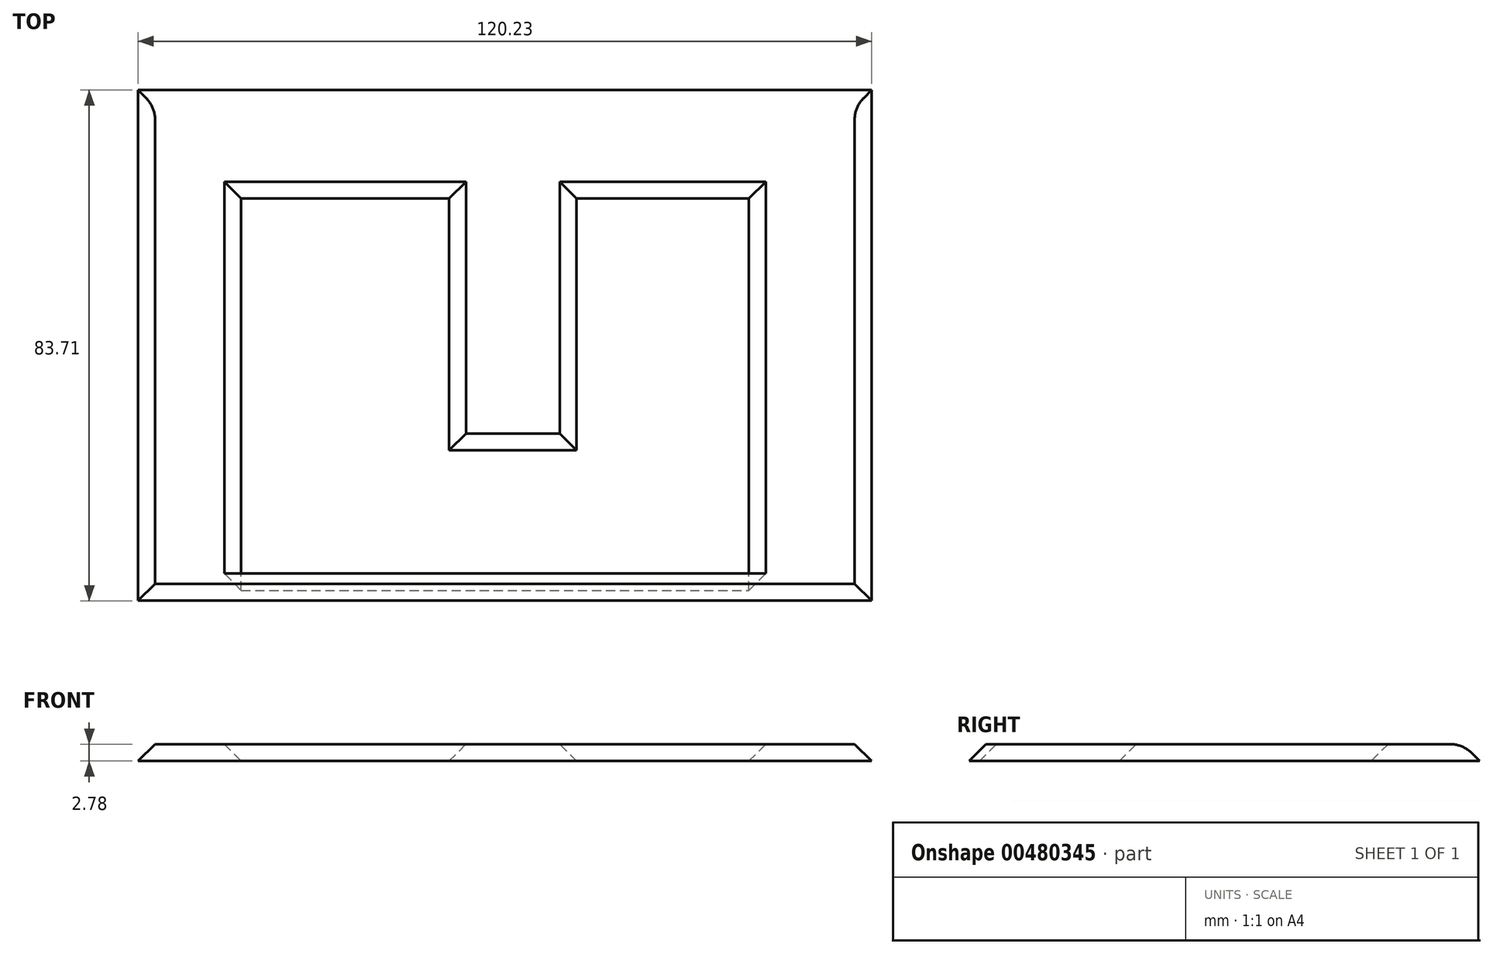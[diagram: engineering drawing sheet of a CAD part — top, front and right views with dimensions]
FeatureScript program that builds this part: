
annotation { "Feature Type Name" : "Feature", "Feature Type Description" : "" }
export const myFeature = defineFeature(function(context is Context, id is Id, definition is map)
    precondition{}
    {
        {
            var Q0;
            Q0=qCreatedBy(makeId("Top.planeOp"),FACE);
            var sketch = newSketch(context, id + "F0", { "sketchPlane" : qUnion([Q0])});
            skLineSegment(sketch, "E0.bottom", {"start": v(-59.68, 46.88) * mm, "end": v(65.17, 46.88) * mm});
            skLineSegment(sketch, "E0.top", {"start": v(-59.68, -41.44) * mm, "end": v(65.17, -41.44) * mm});
            skLineSegment(sketch, "E0.left", {"start": v(-59.68, 46.88) * mm, "end": v(-59.68, -41.44) * mm});
            skLineSegment(sketch, "E0.right", {"start": v(65.17, 46.88) * mm, "end": v(65.17, -41.44) * mm});
            skLineSegment(sketch, "E1.bottom", {"start": v(-38.17, 24.48) * mm, "end": v(-8.71, 24.48) * mm});
            skLineSegment(sketch, "E1.top", {"start": v(-38.17, -32.36) * mm, "end": v(40.45, -32.36) * mm});
            skLineSegment(sketch, "E1.left", {"start": v(-38.17, 24.48) * mm, "end": v(-38.17, -32.36) * mm});
            skLineSegment(sketch, "E1.right", {"start": v(40.45, 24.48) * mm, "end": v(40.45, -32.36) * mm});
            skLineSegment(sketch, "E2.top", {"start": v(-8.71, -16.8) * mm, "end": v(16.8, -16.8) * mm});
            skLineSegment(sketch, "E2.left", {"start": v(-8.71, 24.48) * mm, "end": v(-8.71, -16.8) * mm});
            skLineSegment(sketch, "E2.right", {"start": v(16.8, 24.48) * mm, "end": v(16.8, -16.8) * mm});
            skLineSegment(sketch, "E3.trimOffspring", {"start": v(16.8, 24.48) * mm, "end": v(40.45, 24.48) * mm});
            skSolve(sketch);
        }
        {
            var Q0;
            Q0=makeQuery(id+"F0.imprint","IMPRINT",FACE,{"disambiguationData":[TD([[makeQuery(id+"F0.imprint","IMPRINT",EDGE,{"derivedFrom":sQuery(id+"F0.wireOp",EDGE,"E0.bottom")}),-1.0]])]});
            extrude(context, id + "F1", {"entities" : qUnion([Q0]), "depth" : 2.78 * mm});
        }
        {
            var Q0;
            Q0=makeQuery(id+"F1.opExtrude","CAP_EDGE",EDGE,{"disambiguationData":[OSD([sQuery(id+"F0.wireOp",EDGE,"E0.right")])],"isStart":false});
            chamfer(context, id + "F2", {"entities" : qUnion([Q0]), "width" : 5.08 * mm, "tangentPropagation" : true});
        }
        {
            var Q0;
            Q0=makeQuery(id+"F1.opExtrude","CAP_EDGE",EDGE,{"disambiguationData":[OSD([sQuery(id+"F0.wireOp",EDGE,"E0.bottom")])],"isStart":false});
            chamfer(context, id + "F3", {"entities" : qUnion([Q0]), "width" : 5.08 * mm, "tangentPropagation" : true});
        }
        {
            var Q0;
            Q0=makeQuery(id+"F1.opExtrude","CAP_EDGE",EDGE,{"disambiguationData":[OSD([sQuery(id+"F0.wireOp",EDGE,"E0.left")])],"isStart":false});
            chamfer(context, id + "F4", {"entities" : qUnion([Q0]), "width" : 5.08 * mm, "tangentPropagation" : true});
        }
        {
            var Q0;
            Q0=makeQuery(id+"F1.opExtrude","CAP_EDGE",EDGE,{"disambiguationData":[OSD([sQuery(id+"F0.wireOp",EDGE,"E0.top")])],"isStart":false});
            chamfer(context, id + "F5", {"entities" : qUnion([Q0]), "width" : 5.08 * mm, "tangentPropagation" : true});
        }
        {
            var Q0;
            {var subQ0=sQuery(id+"F0.wireOp",EDGE,"E0.bottom");Q0=makeQuery(id+"F3.opChamfer","BLEND_EDGE",EDGE,{"blendedFrom":[makeQuery(id+"F1.opExtrude","CAP_EDGE",EDGE,{"disambiguationData":[OSD([subQ0])],"isStart":false}),makeQuery(id+"F1.opExtrude","CAP_FACE",FACE,{"disambiguationData":[OSD([subQ0,sQuery(id+"F0.wireOp",EDGE,"E0.top"),sQuery(id+"F0.wireOp",EDGE,"E0.left"),sQuery(id+"F0.wireOp",EDGE,"E0.right"),sQuery(id+"F0.wireOp",EDGE,"E1.bottom"),sQuery(id+"F0.wireOp",EDGE,"E1.top"),sQuery(id+"F0.wireOp",EDGE,"E1.left"),sQuery(id+"F0.wireOp",EDGE,"E1.right"),sQuery(id+"F0.wireOp",EDGE,"E2.top"),sQuery(id+"F0.wireOp",EDGE,"E2.left"),sQuery(id+"F0.wireOp",EDGE,"E2.right"),sQuery(id+"F0.wireOp",EDGE,"E3.trimOffspring")])],"isStart":false})],"blendedInto":[makeQuery(id+"F1.opExtrude","CAP_FACE",FACE,{"disambiguationData":[OSD([subQ0,sQuery(id+"F0.wireOp",EDGE,"E0.top"),sQuery(id+"F0.wireOp",EDGE,"E0.left"),sQuery(id+"F0.wireOp",EDGE,"E0.right"),sQuery(id+"F0.wireOp",EDGE,"E1.bottom"),sQuery(id+"F0.wireOp",EDGE,"E1.top"),sQuery(id+"F0.wireOp",EDGE,"E1.left"),sQuery(id+"F0.wireOp",EDGE,"E1.right"),sQuery(id+"F0.wireOp",EDGE,"E2.top"),sQuery(id+"F0.wireOp",EDGE,"E2.left"),sQuery(id+"F0.wireOp",EDGE,"E2.right"),sQuery(id+"F0.wireOp",EDGE,"E3.trimOffspring")])],"isStart":false})]});}
            fillet(context, id + "F6", {"entities" : qUnion([Q0]), "radius" : 5.08 * mm, "tangentPropagation" : true, "allowEdgeOverflow" : false});
        }
        {
            var Q0;
            Q0=makeQuery(id+"F1.opExtrude","CAP_EDGE",EDGE,{"disambiguationData":[OSD([sQuery(id+"F0.wireOp",EDGE,"E1.left")])],"isStart":false});
            chamfer(context, id + "F7", {"entities" : qUnion([Q0]), "width" : 5.08 * mm, "tangentPropagation" : true});
        }
        {
            var Q0;
            Q0=makeQuery(id+"F1.opExtrude","CAP_EDGE",EDGE,{"disambiguationData":[OSD([sQuery(id+"F0.wireOp",EDGE,"E3.trimOffspring")])],"isStart":false});
            chamfer(context, id + "F8", {"entities" : qUnion([Q0]), "width" : 5.08 * mm, "tangentPropagation" : true});
        }
        {
            var Q0;
            Q0=makeQuery(id+"F1.opExtrude","CAP_EDGE",EDGE,{"disambiguationData":[OSD([sQuery(id+"F0.wireOp",EDGE,"E1.bottom")])],"isStart":false});
            chamfer(context, id + "F9", {"entities" : qUnion([Q0]), "width" : 5.08 * mm, "tangentPropagation" : true});
        }
        {
            var Q0;
            Q0=makeQuery(id+"F1.opExtrude","CAP_EDGE",EDGE,{"disambiguationData":[OSD([sQuery(id+"F0.wireOp",EDGE,"E2.left")])],"isStart":false});
            chamfer(context, id + "F10", {"entities" : qUnion([Q0]), "width" : 5.08 * mm, "tangentPropagation" : true});
        }
        {
            var Q0;
            Q0=makeQuery(id+"F1.opExtrude","CAP_EDGE",EDGE,{"disambiguationData":[OSD([sQuery(id+"F0.wireOp",EDGE,"E2.right")])],"isStart":false});
            chamfer(context, id + "F11", {"entities" : qUnion([Q0]), "width" : 5.08 * mm, "tangentPropagation" : true});
        }
        {
            var Q0;
            Q0=makeQuery(id+"F1.opExtrude","CAP_EDGE",EDGE,{"disambiguationData":[OSD([sQuery(id+"F0.wireOp",EDGE,"E1.right")])],"isStart":false});
            chamfer(context, id + "F12", {"entities" : qUnion([Q0]), "width" : 5.08 * mm, "tangentPropagation" : true});
        }
        {
            var Q0;
            Q0=makeQuery(id+"F1.opExtrude","CAP_EDGE",EDGE,{"disambiguationData":[OSD([sQuery(id+"F0.wireOp",EDGE,"E2.top")])],"isStart":false});
            chamfer(context, id + "F13", {"entities" : qUnion([Q0]), "width" : 5.08 * mm, "tangentPropagation" : true});
        }
        {
            var Q0;
            Q0=makeQuery(id+"F1.opExtrude","CAP_EDGE",EDGE,{"disambiguationData":[OSD([sQuery(id+"F0.wireOp",EDGE,"E1.top")])],"isStart":true});
            chamfer(context, id + "F14", {"entities" : qUnion([Q0]), "width" : 5.08 * mm, "tangentPropagation" : true});
        }
    });
